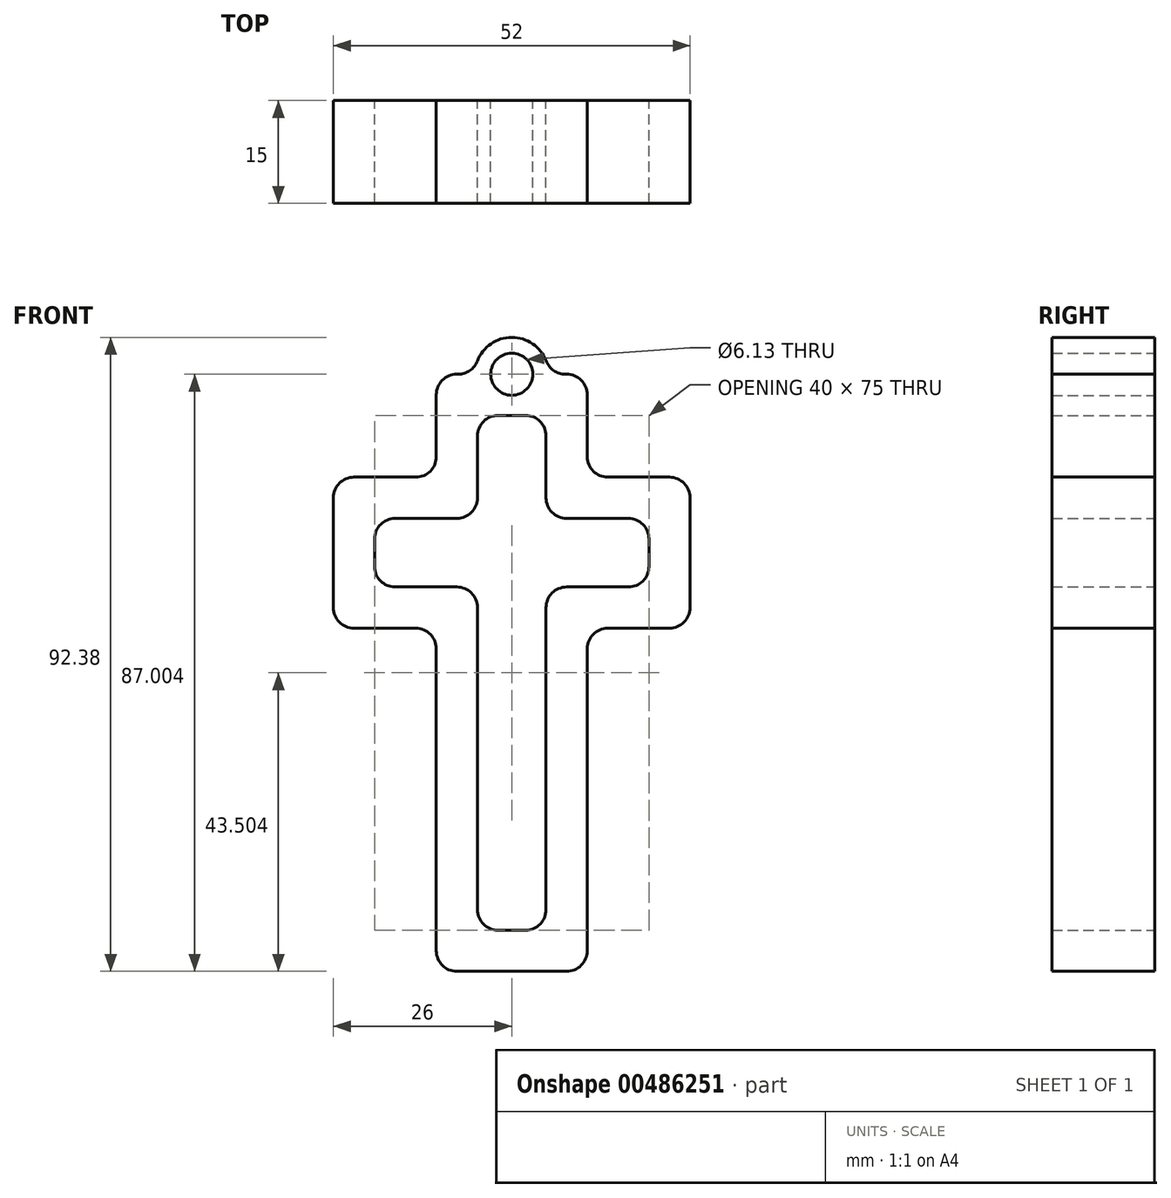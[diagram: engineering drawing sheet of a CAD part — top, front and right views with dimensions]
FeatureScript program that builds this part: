
annotation { "Feature Type Name" : "Feature", "Feature Type Description" : "" }
export const myFeature = defineFeature(function(context is Context, id is Id, definition is map)
    precondition{}
    {
        {
            var Q0;
            Q0=qCreatedBy(makeId("Front.planeOp"),FACE);
            var sketch = newSketch(context, id + "F0", { "sketchPlane" : qUnion([Q0])});
            skLineSegment(sketch, "E0", {"start": v(0, 58.13) * mm, "end": v(-10, 58.13) * mm});
            skLineSegment(sketch, "E1", {"start": v(-10, -16.87) * mm, "end": v(0, -16.87) * mm});
            skLineSegment(sketch, "E2", {"start": v(-10, 58.13) * mm, "end": v(-10, 43.13) * mm});
            skLineSegment(sketch, "E3", {"start": v(-10, 43.13) * mm, "end": v(-25, 43.13) * mm});
            skLineSegment(sketch, "E4", {"start": v(-25, 43.13) * mm, "end": v(-25, 33.13) * mm});
            skLineSegment(sketch, "E5", {"start": v(-25, 33.13) * mm, "end": v(-10, 33.13) * mm});
            skLineSegment(sketch, "E6", {"start": v(0, 43.13) * mm, "end": v(15, 43.13) * mm});
            skLineSegment(sketch, "E7", {"start": v(0, 33.13) * mm, "end": v(15, 33.13) * mm});
            skLineSegment(sketch, "E8", {"start": v(15, 43.13) * mm, "end": v(15, 33.13) * mm});
            skLineSegment(sketch, "E9", {"start": v(-10, 33.13) * mm, "end": v(-10, -16.87) * mm});
            skLineSegment(sketch, "E10", {"start": v(0, 58.13) * mm, "end": v(0, 43.13) * mm});
            skLineSegment(sketch, "E11", {"start": v(0, 33.13) * mm, "end": v(0, -16.87) * mm});
            skLineSegment(sketch, "E12", {"start": v(-16, -16.87) * mm, "end": v(-16, -22.87) * mm});
            skLineSegment(sketch, "E13", {"start": v(-16, -22.87) * mm, "end": v(6, -22.87) * mm});
            skLineSegment(sketch, "E14", {"start": v(-25, 27.13) * mm, "end": v(-16, 27.13) * mm});
            skLineSegment(sketch, "E15", {"start": v(-16, -16.87) * mm, "end": v(-16, 27.13) * mm});
            skLineSegment(sketch, "E16", {"start": v(6, -22.87) * mm, "end": v(6, 27.13) * mm});
            skLineSegment(sketch, "E17", {"start": v(6, 27.13) * mm, "end": v(15, 27.13) * mm});
            skLineSegment(sketch, "E18", {"start": v(15, 27.13) * mm, "end": v(21, 27.13) * mm});
            skLineSegment(sketch, "E19", {"start": v(21, 49.13) * mm, "end": v(6, 49.13) * mm});
            skLineSegment(sketch, "E20", {"start": v(6, 49.13) * mm, "end": v(6, 64.13) * mm});
            skLineSegment(sketch, "E21", {"start": v(6, 64.13) * mm, "end": v(-16, 64.13) * mm});
            skLineSegment(sketch, "E22", {"start": v(-16, 64.13) * mm, "end": v(-16, 49.13) * mm});
            skLineSegment(sketch, "E23", {"start": v(-16, 49.13) * mm, "end": v(-31, 49.13) * mm});
            skLineSegment(sketch, "E24", {"start": v(-31, 27.13) * mm, "end": v(-25, 27.13) * mm});
            skLineSegment(sketch, "E25", {"start": v(-16, 64.13) * mm, "end": v(-5, 64.13) * mm});
            skCircle(sketch, "E26", {"center": v(-5, 64.13) * mm, "radius": 5.37 * mm});
            skCircle(sketch, "E27", {"center": v(-5, 64.13) * mm, "radius": 3.07 * mm});
            skLineSegment(sketch, "E28", {"start": v(-5, 64.13) * mm, "end": v(-5, -22.87) * mm, "construction": true});
            skLineSegment(sketch, "E29", {"start": v(-31, 49.13) * mm, "end": v(-31, 27.13) * mm});
            skLineSegment(sketch, "E30", {"start": v(21, 49.13) * mm, "end": v(21, 27.13) * mm});
            skSolve(sketch);
        }
        {
            var Q0;
            Q0=qSketchRegion(id+"F0",true);
            extrude(context, id + "F1", {"entities" : qUnion([Q0]), "depth" : 15 * mm});
        }
        {
            var Q0;
            Q0=makeQuery(id+"F1.opExtrude","SWEPT_EDGE",EDGE,{"disambiguationData":[OSD([sQuery(id+"F0.wireOp",EDGE,"E1"),sQuery(id+"F0.wireOp",EDGE,"E9"),sQuery(id+"F0.wireOp",EDGE,"SoNozwRW-mJtI-os8s-alWq-0gxmPMuzM5nE"),sQuery(id+"F0.wireOp",EDGE,"zj1N1qql-69xp-IFOC-AOg6-64gHm7Rjqr0n")])]});
            var Q1;
            Q1=makeQuery(id+"F1.opExtrude","SWEPT_EDGE",EDGE,{"disambiguationData":[OSD([sQuery(id+"F0.wireOp",EDGE,"E5"),sQuery(id+"F0.wireOp",EDGE,"E9")])]});
            var Q2;
            Q2=makeQuery(id+"F1.opExtrude","SWEPT_EDGE",EDGE,{"disambiguationData":[OSD([sQuery(id+"F0.wireOp",EDGE,"E4"),sQuery(id+"F0.wireOp",EDGE,"E5"),sQuery(id+"F0.wireOp",EDGE,"JkkYBlIC-WK7h-VhNU-eD4w-PFI7T7pZ055c")])]});
            var Q3;
            Q3=makeQuery(id+"F1.opExtrude","SWEPT_EDGE",EDGE,{"disambiguationData":[OSD([sQuery(id+"F0.wireOp",EDGE,"E1"),sQuery(id+"F0.wireOp",EDGE,"E11"),sQuery(id+"F0.wireOp",EDGE,"p5YPYbok-UCxx-zQt2-bGdL-7y8e1GDendUJ"),sQuery(id+"F0.wireOp",EDGE,"QCRdUmlX-UTfE-SmZh-7q9e-hv5Va6i25oJJ")])]});
            var Q4;
            Q4=makeQuery(id+"F1.opExtrude","SWEPT_EDGE",EDGE,{"disambiguationData":[OSD([sQuery(id+"F0.wireOp",EDGE,"E7"),sQuery(id+"F0.wireOp",EDGE,"E11")])]});
            var Q5;
            Q5=makeQuery(id+"F1.opExtrude","SWEPT_EDGE",EDGE,{"disambiguationData":[OSD([sQuery(id+"F0.wireOp",EDGE,"E7"),sQuery(id+"F0.wireOp",EDGE,"E8"),sQuery(id+"F0.wireOp",EDGE,"M5XVuVZv-HyxV-EBHI-0UWz-zm9aioapNkRY"),sQuery(id+"F0.wireOp",EDGE,"HJXAKwE1-8RYy-Ky9X-1OAD-b5Pzt5JmRXUv")])]});
            var Q6;
            Q6=makeQuery(id+"F1.opExtrude","SWEPT_EDGE",EDGE,{"disambiguationData":[OSD([sQuery(id+"F0.wireOp",EDGE,"E6"),sQuery(id+"F0.wireOp",EDGE,"E8"),sQuery(id+"F0.wireOp",EDGE,"t1L3Ds75-5ZQ1-6rzq-zuNa-BfBlgHZkFqex"),sQuery(id+"F0.wireOp",EDGE,"EY3CKX2p-qQSQ-HcfL-y7fS-CjnnHh3G8Awt")])]});
            var Q7;
            Q7=makeQuery(id+"F1.opExtrude","SWEPT_EDGE",EDGE,{"disambiguationData":[OSD([sQuery(id+"F0.wireOp",EDGE,"E6"),sQuery(id+"F0.wireOp",EDGE,"E10")])]});
            var Q8;
            Q8=makeQuery(id+"F1.opExtrude","SWEPT_EDGE",EDGE,{"disambiguationData":[OSD([sQuery(id+"F0.wireOp",EDGE,"E0"),sQuery(id+"F0.wireOp",EDGE,"E10")])]});
            var Q9;
            Q9=makeQuery(id+"F1.opExtrude","SWEPT_EDGE",EDGE,{"disambiguationData":[OSD([sQuery(id+"F0.wireOp",EDGE,"E0"),sQuery(id+"F0.wireOp",EDGE,"E2")])]});
            var Q10;
            Q10=makeQuery(id+"F1.opExtrude","SWEPT_EDGE",EDGE,{"disambiguationData":[OSD([sQuery(id+"F0.wireOp",EDGE,"E2"),sQuery(id+"F0.wireOp",EDGE,"E3")])]});
            var Q11;
            Q11=makeQuery(id+"F1.opExtrude","SWEPT_EDGE",EDGE,{"disambiguationData":[OSD([sQuery(id+"F0.wireOp",EDGE,"E3"),sQuery(id+"F0.wireOp",EDGE,"E4")])]});
            fillet(context, id + "F2", {"entities" : qUnion([Q0, Q1, Q2, Q3, Q4, Q5, Q6, Q7, Q8, Q9, Q10, Q11]), "radius" : 3 * mm, "tangentPropagation" : true, "allowEdgeOverflow" : false});
        }
        {
            var Q0;
            Q0=makeQuery(id+"F1.opExtrude","SWEPT_EDGE",EDGE,{"disambiguationData":[OSD([sQuery(id+"F0.wireOp",EDGE,"E19"),sQuery(id+"F0.wireOp",EDGE,"E20")])]});
            fillet(context, id + "F3", {"entities" : qUnion([Q0]), "radius" : 3 * mm, "tangentPropagation" : true, "allowEdgeOverflow" : false});
        }
        {
            var Q0;
            Q0=makeQuery(id+"F1.opExtrude","SWEPT_EDGE",EDGE,{"disambiguationData":[OSD([sQuery(id+"F0.wireOp",EDGE,"E20"),sQuery(id+"F0.wireOp",EDGE,"E21")])]});
            var Q1;
            Q1=makeQuery(id+"F1.opExtrude","SWEPT_EDGE",EDGE,{"disambiguationData":[OSD([sQuery(id+"F0.wireOp",EDGE,"E21"),sQuery(id+"F0.wireOp",EDGE,"E26")])]});
            var Q2;
            Q2=makeQuery(id+"F1.opExtrude","SWEPT_EDGE",EDGE,{"disambiguationData":[OSD([sQuery(id+"F0.wireOp",EDGE,"sMuBDEL5-hzGn-YPGm-qX1Y-40NOGYWRmCt9"),sQuery(id+"F0.wireOp",EDGE,"E19")])]});
            var Q3;
            Q3=makeQuery(id+"F1.opExtrude","SWEPT_EDGE",EDGE,{"disambiguationData":[OSD([sQuery(id+"F0.wireOp",EDGE,"E18"),sQuery(id+"F0.wireOp",EDGE,"sMuBDEL5-hzGn-YPGm-qX1Y-40NOGYWRmCt9")])]});
            var Q4;
            Q4=makeQuery(id+"F1.opExtrude","SWEPT_EDGE",EDGE,{"disambiguationData":[OSD([sQuery(id+"F0.wireOp",EDGE,"E16"),sQuery(id+"F0.wireOp",EDGE,"E17")])]});
            var Q5;
            Q5=makeQuery(id+"F1.opExtrude","SWEPT_EDGE",EDGE,{"disambiguationData":[OSD([sQuery(id+"F0.wireOp",EDGE,"E13"),sQuery(id+"F0.wireOp",EDGE,"E16")])]});
            var Q6;
            Q6=makeQuery(id+"F1.opExtrude","SWEPT_EDGE",EDGE,{"disambiguationData":[OSD([sQuery(id+"F0.wireOp",EDGE,"E12"),sQuery(id+"F0.wireOp",EDGE,"E13")])]});
            var Q7;
            Q7=makeQuery(id+"F1.opExtrude","SWEPT_EDGE",EDGE,{"disambiguationData":[OSD([sQuery(id+"F0.wireOp",EDGE,"E14"),sQuery(id+"F0.wireOp",EDGE,"E15")])]});
            var Q8;
            Q8=makeQuery(id+"F1.opExtrude","SWEPT_EDGE",EDGE,{"disambiguationData":[OSD([sQuery(id+"F0.wireOp",EDGE,"2tCYhLwo-kV1n-wEjR-YmM0-9tpOZI8bn5kh"),sQuery(id+"F0.wireOp",EDGE,"E24")])]});
            var Q9;
            Q9=makeQuery(id+"F1.opExtrude","SWEPT_EDGE",EDGE,{"disambiguationData":[OSD([sQuery(id+"F0.wireOp",EDGE,"E23"),sQuery(id+"F0.wireOp",EDGE,"2tCYhLwo-kV1n-wEjR-YmM0-9tpOZI8bn5kh")])]});
            var Q10;
            Q10=makeQuery(id+"F1.opExtrude","SWEPT_EDGE",EDGE,{"disambiguationData":[OSD([sQuery(id+"F0.wireOp",EDGE,"E25"),sQuery(id+"F0.wireOp",EDGE,"E26")])]});
            var Q11;
            Q11=makeQuery(id+"F1.opExtrude","SWEPT_EDGE",EDGE,{"disambiguationData":[OSD([sQuery(id+"F0.wireOp",EDGE,"E22"),sQuery(id+"F0.wireOp",EDGE,"E25")])]});
            var Q12;
            Q12=makeQuery(id+"F1.opExtrude","SWEPT_EDGE",EDGE,{"disambiguationData":[OSD([sQuery(id+"F0.wireOp",EDGE,"E22"),sQuery(id+"F0.wireOp",EDGE,"E23")])]});
            fillet(context, id + "F4", {"entities" : qUnion([Q0, Q1, Q2, Q3, Q4, Q5, Q6, Q7, Q8, Q9, Q10, Q11, Q12]), "radius" : 3 * mm, "tangentPropagation" : true, "allowEdgeOverflow" : false});
        }
    });
